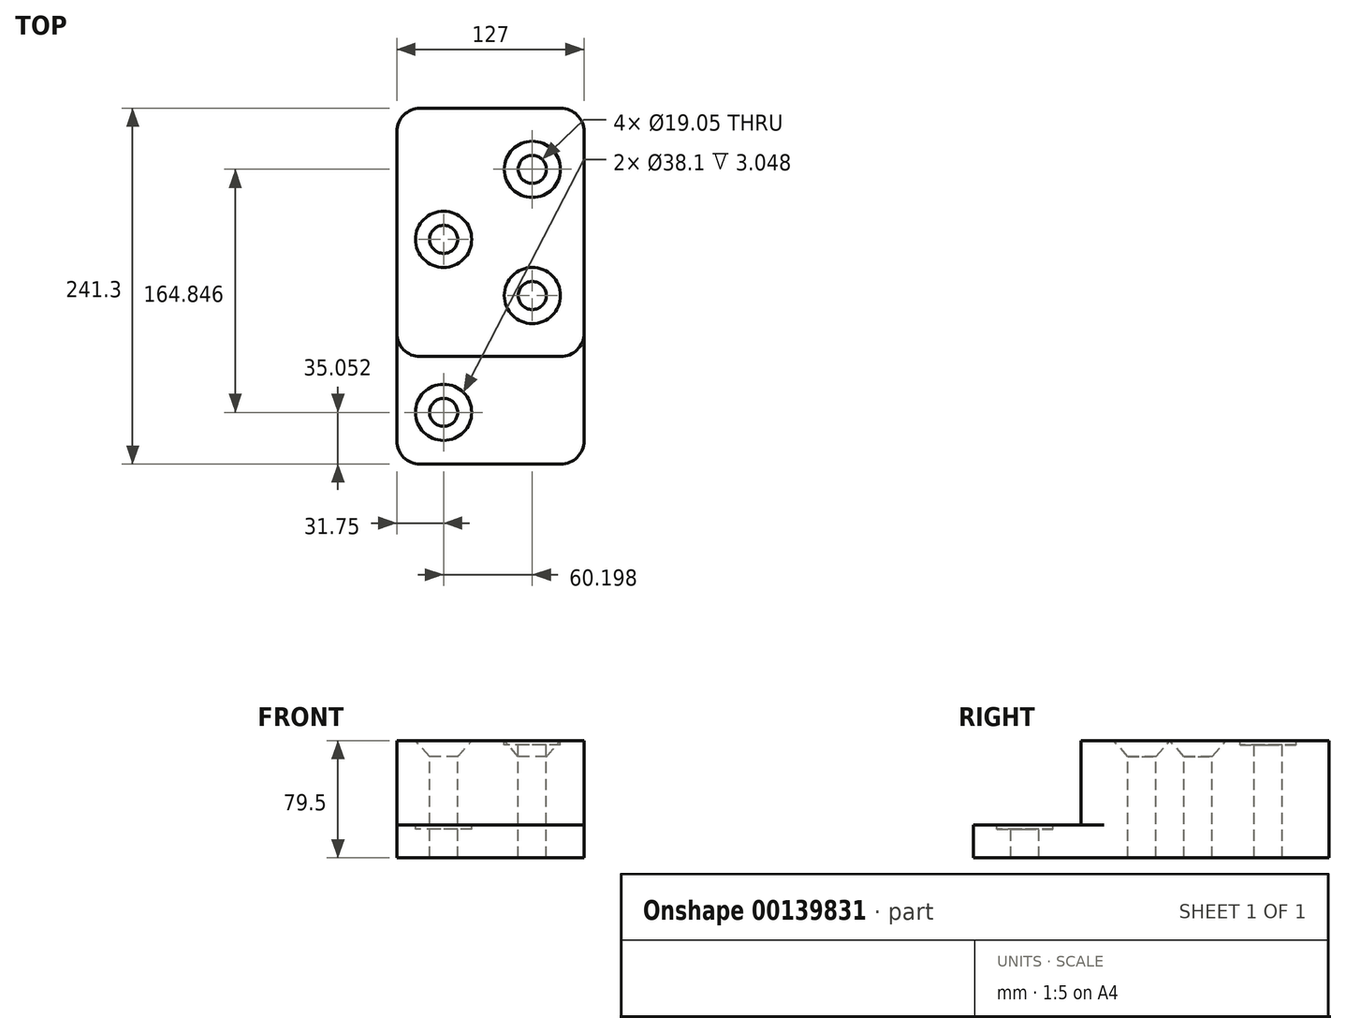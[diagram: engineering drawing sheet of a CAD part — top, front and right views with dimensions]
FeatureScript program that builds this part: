
annotation { "Feature Type Name" : "Feature", "Feature Type Description" : "" }
export const myFeature = defineFeature(function(context is Context, id is Id, definition is map)
    precondition{}
    {
        {
            var Q0;
            Q0=qCreatedBy(makeId("Right.planeOp"),FACE);
            var sketch = newSketch(context, id + "F0", { "sketchPlane" : qUnion([Q0])});
            skLineSegment(sketch, "E0", {"start": v(-120.65, 22.35) * mm, "end": v(-120.65, 0) * mm});
            skLineSegment(sketch, "E1", {"start": v(-120.65, 0) * mm, "end": v(120.65, 0) * mm});
            skLineSegment(sketch, "E2", {"start": v(120.65, 0) * mm, "end": v(120.65, 79.5) * mm});
            skLineSegment(sketch, "E3", {"start": v(120.65, 79.5) * mm, "end": v(-47.75, 79.5) * mm});
            skLineSegment(sketch, "E4", {"start": v(-47.75, 79.5) * mm, "end": v(-47.75, 22.35) * mm});
            skLineSegment(sketch, "E5", {"start": v(-47.75, 22.35) * mm, "end": v(-120.65, 22.35) * mm});
            skLineSegment(sketch, "E6", {"start": v(0, 111.95) * mm, "end": v(0, -47.52) * mm, "construction": true});
            skSolve(sketch);
        }
        {
            var Q0;
            Q0=makeQuery(id+"F0.imprint","IMPRINT",FACE,{"disambiguationData":[TD([[makeQuery(id+"F0.imprint","IMPRINT",EDGE,{"derivedFrom":sQuery(id+"F0.wireOp",EDGE,"E0")}),1.0]])]});
            extrude(context, id + "F1", {"entities" : qUnion([Q0]), "endBound" : BoundingType.SYMMETRIC, "depth" : 127 * mm});
        }
        {
            var Q0;
            Q0=makeQuery(id+"F1.opExtrude","CAP_EDGE",EDGE,{"disambiguationData":[OSD([sQuery(id+"F0.wireOp",EDGE,"E4")])],"isStart":false});
            var Q1;
            Q1=makeQuery(id+"F1.opExtrude","CAP_EDGE",EDGE,{"disambiguationData":[OSD([sQuery(id+"F0.wireOp",EDGE,"E4")])],"isStart":true});
            var Q2;
            Q2=makeQuery(id+"F1.opExtrude","CAP_EDGE",EDGE,{"disambiguationData":[OSD([sQuery(id+"F0.wireOp",EDGE,"E0")])],"isStart":false});
            var Q3;
            Q3=makeQuery(id+"F1.opExtrude","CAP_EDGE",EDGE,{"disambiguationData":[OSD([sQuery(id+"F0.wireOp",EDGE,"E0")])],"isStart":true});
            var Q4;
            Q4=makeQuery(id+"F1.opExtrude","CAP_EDGE",EDGE,{"disambiguationData":[OSD([sQuery(id+"F0.wireOp",EDGE,"E2")])],"isStart":false});
            var Q5;
            Q5=makeQuery(id+"F1.opExtrude","CAP_EDGE",EDGE,{"disambiguationData":[OSD([sQuery(id+"F0.wireOp",EDGE,"E2")])],"isStart":true});
            fillet(context, id + "F2", {"entities" : qUnion([Q0, Q1, Q2, Q3, Q4, Q5]), "radius" : 15.75 * mm, "tangentPropagation" : true, "allowEdgeOverflow" : false});
        }
        {
            var Q0;
            Q0=makeQuery(id+"F1.opExtrude","SWEPT_FACE",FACE,{"disambiguationData":[OSD([sQuery(id+"F0.wireOp",EDGE,"E5")])]});
            var sketch = newSketch(context, id + "F3", { "sketchPlane" : qUnion([Q0])});
            skPoint(sketch, "E7", {"position": v(-31.75, -85.6) * mm});
            skSolve(sketch);
        }
        {
            var Q0;
            Q0=makeQuery(id+"F1.opExtrude","SWEPT_FACE",FACE,{"disambiguationData":[OSD([sQuery(id+"F0.wireOp",EDGE,"E3")])]});
            var sketch = newSketch(context, id + "F4", { "sketchPlane" : qUnion([Q0])});
            skPoint(sketch, "E8", {"position": v(28.45, 79.25) * mm});
            skPoint(sketch, "E9", {"position": v(28.45, -6.35) * mm});
            skPoint(sketch, "E10", {"position": v(-31.75, 31.75) * mm});
            skSolve(sketch);
        }
        {
            var Q0;
            Q0=sQuery(id+"F3.wireOp",VERTEX,"E7");
            var Q1;
            Q1=sQuery(id+"F4.wireOp",VERTEX,"E8");
            var Q2;
            Q2=makeQuery(id+"F1.opExtrude","SWEPT_BODY",BODY,{"disambiguationData":[OSD([sQuery(id+"F0.wireOp",EDGE,"E0"),sQuery(id+"F0.wireOp",EDGE,"E1"),sQuery(id+"F0.wireOp",EDGE,"E2"),sQuery(id+"F0.wireOp",EDGE,"E3"),sQuery(id+"F0.wireOp",EDGE,"E4"),sQuery(id+"F0.wireOp",EDGE,"E5")])]});
            hole(context, id + "F5", {"style" : HoleStyle.C_BORE, "endStyle" : HoleEndStyle.THROUGH, "holeDiameter" : 19.05 * mm, "cBoreDiameter" : 38.1 * mm, "cBoreDepth" : 3.05 * mm, "locations" : qUnion([Q0, Q1]), "scope" : qUnion([Q2]), "isTappedThrough" : true});
        }
        {
            var Q0;
            Q0=sQuery(id+"F4.wireOp",VERTEX,"E9");
            var Q1;
            Q1=sQuery(id+"F4.wireOp",VERTEX,"E10");
            var Q2;
            Q2=makeQuery(id+"F1.opExtrude","SWEPT_BODY",BODY,{"disambiguationData":[OSD([sQuery(id+"F0.wireOp",EDGE,"E0"),sQuery(id+"F0.wireOp",EDGE,"E1"),sQuery(id+"F0.wireOp",EDGE,"E2"),sQuery(id+"F0.wireOp",EDGE,"E3"),sQuery(id+"F0.wireOp",EDGE,"E4"),sQuery(id+"F0.wireOp",EDGE,"E5")])]});
            hole(context, id + "F6", {"style" : HoleStyle.C_SINK, "endStyle" : HoleEndStyle.THROUGH, "holeDiameter" : 19.05 * mm, "cSinkDiameter" : 38.1 * mm, "cSinkAngle" : 82 * degree, "locations" : qUnion([Q0, Q1]), "scope" : qUnion([Q2]), "isTappedThrough" : true});
        }
    });
